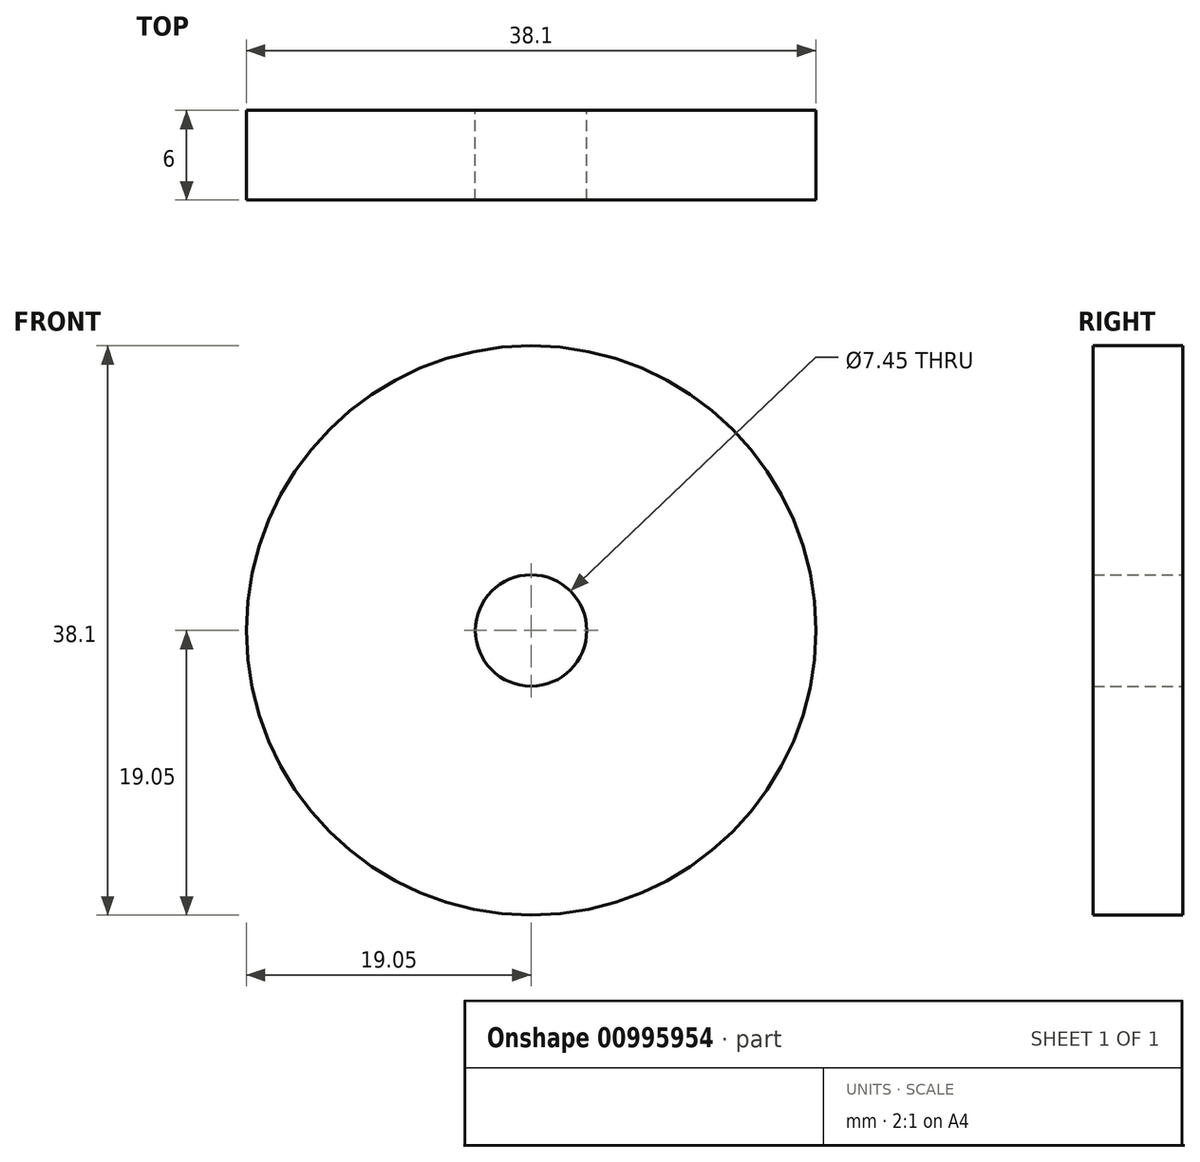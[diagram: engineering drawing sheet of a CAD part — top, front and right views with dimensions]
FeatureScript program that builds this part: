
annotation { "Feature Type Name" : "Feature", "Feature Type Description" : "" }
export const myFeature = defineFeature(function(context is Context, id is Id, definition is map)
    precondition{}
    {
        {
            var Q0;
            Q0=qCreatedBy(makeId("Front.planeOp"),FACE);
            var sketch = newSketch(context, id + "F0", { "sketchPlane" : qUnion([Q0])});
            skCircle(sketch, "E0", {"center": v(0, 0) * mm, "radius": 19.05 * mm});
            skCircle(sketch, "E1", {"center": v(0, 0) * mm, "radius": 3.73 * mm});
            skSolve(sketch);
        }
        {
            var Q0;
            Q0 = qSketchRegion(id + "F0", true);
            extrude(context, id + "F1", {"entities" : qUnion([Q0]), "endBound" : BoundingType.SYMMETRIC, "depth" : 6 * mm, "offsetDistance" : 25.4 * mm});
        }
    });
